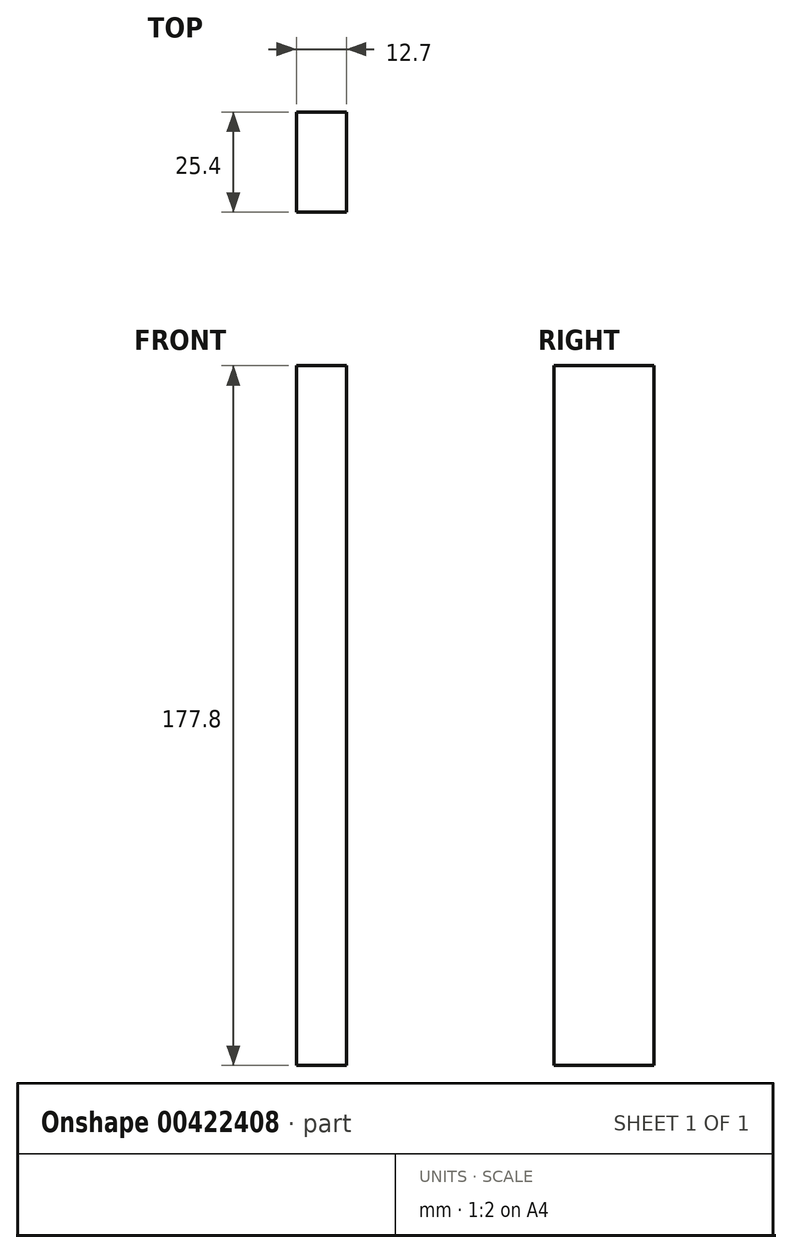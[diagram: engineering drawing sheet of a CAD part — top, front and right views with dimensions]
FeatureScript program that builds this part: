
annotation { "Feature Type Name" : "Feature", "Feature Type Description" : "" }
export const myFeature = defineFeature(function(context is Context, id is Id, definition is map)
    precondition{}
    {
        {
            var Q0;
            Q0=qCreatedBy(makeId("Top.planeOp"),FACE);
            var sketch = newSketch(context, id + "F0", { "sketchPlane" : qUnion([Q0])});
            skLineSegment(sketch, "E0.bottom", {"start": v(0, 0) * mm, "end": v(12.7, 0) * mm});
            skLineSegment(sketch, "E0.top", {"start": v(0, 25.4) * mm, "end": v(12.7, 25.4) * mm});
            skLineSegment(sketch, "E0.left", {"start": v(0, 0) * mm, "end": v(0, 25.4) * mm});
            skLineSegment(sketch, "E0.right", {"start": v(12.7, 0) * mm, "end": v(12.7, 25.4) * mm});
            skSolve(sketch);
        }
        {
            var Q0;
            Q0 = qSketchRegion(id + "F0", true);
            extrude(context, id + "F1", {"entities" : qUnion([Q0]), "depth" : 177.8 * mm});
        }
    });
